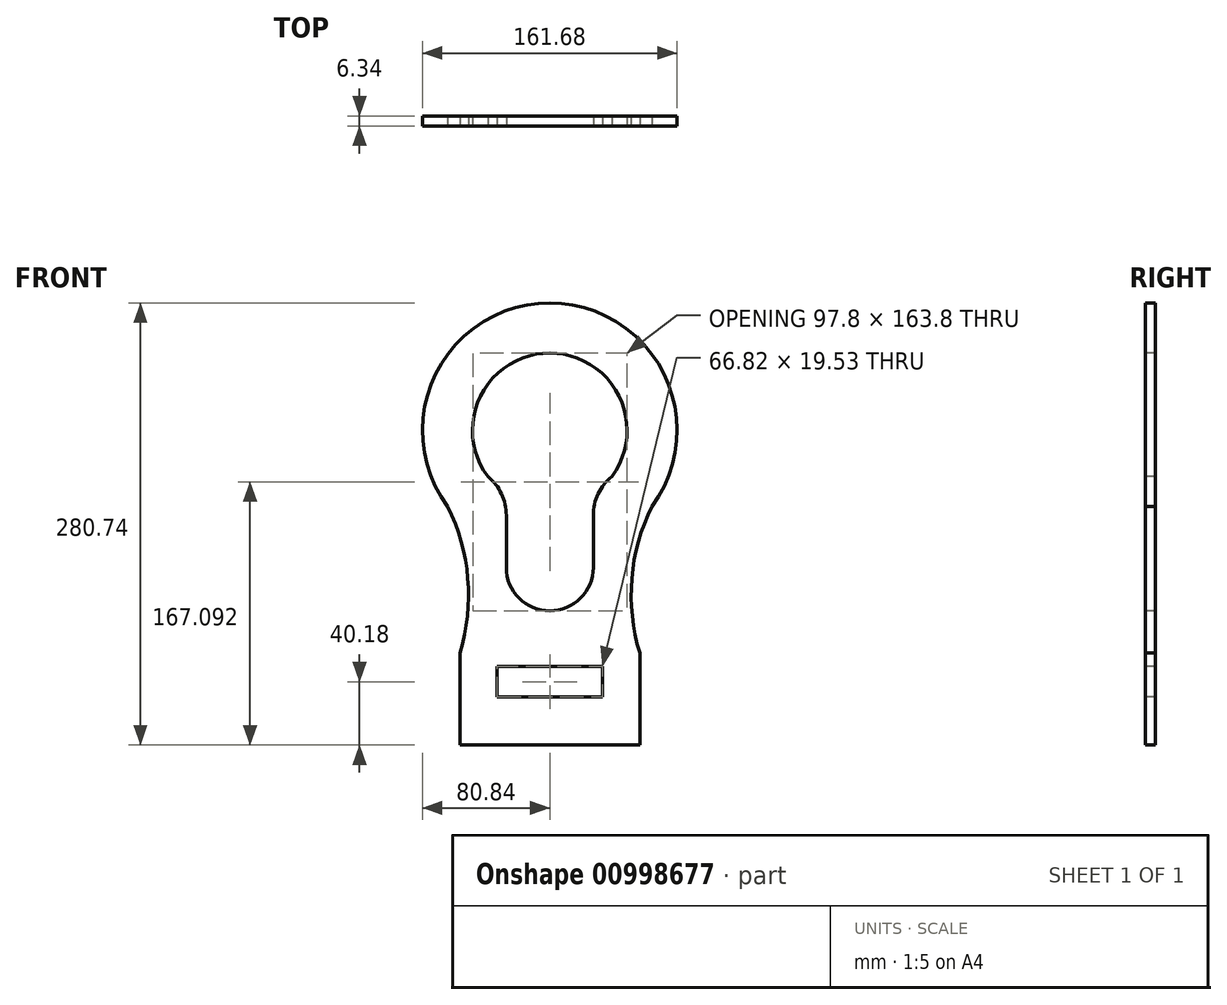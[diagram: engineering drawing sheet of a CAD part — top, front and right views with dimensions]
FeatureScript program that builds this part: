
annotation { "Feature Type Name" : "Feature", "Feature Type Description" : "" }
export const myFeature = defineFeature(function(context is Context, id is Id, definition is map)
    precondition{}
    {
        {
            var Q0;
            Q0=qCreatedBy(makeId("Front.planeOp"),FACE);
            var sketch = newSketch(context, id + "F0", { "sketchPlane" : qUnion([Q0])});
            skLineSegment(sketch, "E0", {"start": v(-57.15, -304.62) * mm, "end": v(-57.15, -246.2) * mm});
            skLineSegment(sketch, "E1", {"start": v(-57.15, -246.2) * mm, "end": v(-57.15, -304.62) * mm});
            skLineSegment(sketch, "E2", {"start": v(-57.15, -304.62) * mm, "end": v(0, -304.62) * mm});
            skArc(sketch, "E3", {"start": v(-57.15, -246.2) * mm, "mid": v(-52.1, -198.88) * mm, "end": v(-64.81, -153.03) * mm});
            skLineSegment(sketch, "E4.MirrorCS", {"start": v(57.15, -304.62) * mm, "end": v(0, -304.62) * mm});
            skArc(sketch, "E5", {"start": v(64.81, -153.03) * mm, "mid": v(0, -23.88) * mm, "end": v(-64.81, -153.03) * mm});
            skLineSegment(sketch, "E6", {"start": v(0, -304.62) * mm, "end": v(0, -104.72) * mm, "construction": true});
            skLineSegment(sketch, "E7.MirrorCS", {"start": v(57.15, -246.2) * mm, "end": v(57.15, -304.62) * mm});
            skArc(sketch, "E8.MirrorCS", {"start": v(57.15, -246.2) * mm, "mid": v(52.1, -198.88) * mm, "end": v(64.81, -153.03) * mm});
            skPoint(sketch, "E9.MirrorCS.end.orphan", {"position": v(139.36, -304.62) * mm});
            skArc(sketch, "E10.0", {"start": v(39.36, -134.06) * mm, "mid": v(0, -55.63) * mm, "end": v(-39.36, -134.06) * mm});
            skLineSegment(sketch, "E11", {"start": v(-27.63, -158.83) * mm, "end": v(-27.63, -191.8) * mm});
            skArc(sketch, "E12", {"start": v(-27.63, -158.83) * mm, "mid": v(-30.71, -145.13) * mm, "end": v(-39.36, -134.06) * mm});
            skLineSegment(sketch, "E13.MirrorCS", {"start": v(27.63, -158.83) * mm, "end": v(27.63, -191.8) * mm});
            skArc(sketch, "E14.MirrorCS", {"start": v(27.63, -158.83) * mm, "mid": v(30.71, -145.13) * mm, "end": v(39.36, -134.06) * mm});
            skArc(sketch, "E15", {"start": v(-27.63, -191.8) * mm, "mid": v(0, -219.43) * mm, "end": v(27.63, -191.8) * mm});
            skLineSegment(sketch, "E16.bottom", {"start": v(33.41, -274.2) * mm, "end": v(-33.41, -274.2) * mm});
            skLineSegment(sketch, "E16.top", {"start": v(33.41, -254.67) * mm, "end": v(-33.41, -254.67) * mm});
            skLineSegment(sketch, "E16.left", {"start": v(33.41, -274.2) * mm, "end": v(33.41, -254.67) * mm});
            skLineSegment(sketch, "E16.right", {"start": v(-33.41, -274.2) * mm, "end": v(-33.41, -254.67) * mm});
            skPoint(sketch, "E16.middle", {"position": v(0, -264.44) * mm});
            skSolve(sketch);
        }
        {
            var Q0;
            Q0=makeQuery(id+"F0.imprint","IMPRINT",FACE,{"disambiguationData":[TD([[makeQuery(id+"F0.imprint","IMPRINT",EDGE,{"derivedFrom":sQuery(id+"F0.wireOp",EDGE,"E0")}),-1.0]])]});
            extrude(context, id + "F1", {"entities" : qUnion([Q0]), "endBound" : BoundingType.SYMMETRIC, "oppositeDirection" : true, "depth" : 6.35 * mm, "offsetDistance" : 25.4 * mm});
        }
    });
